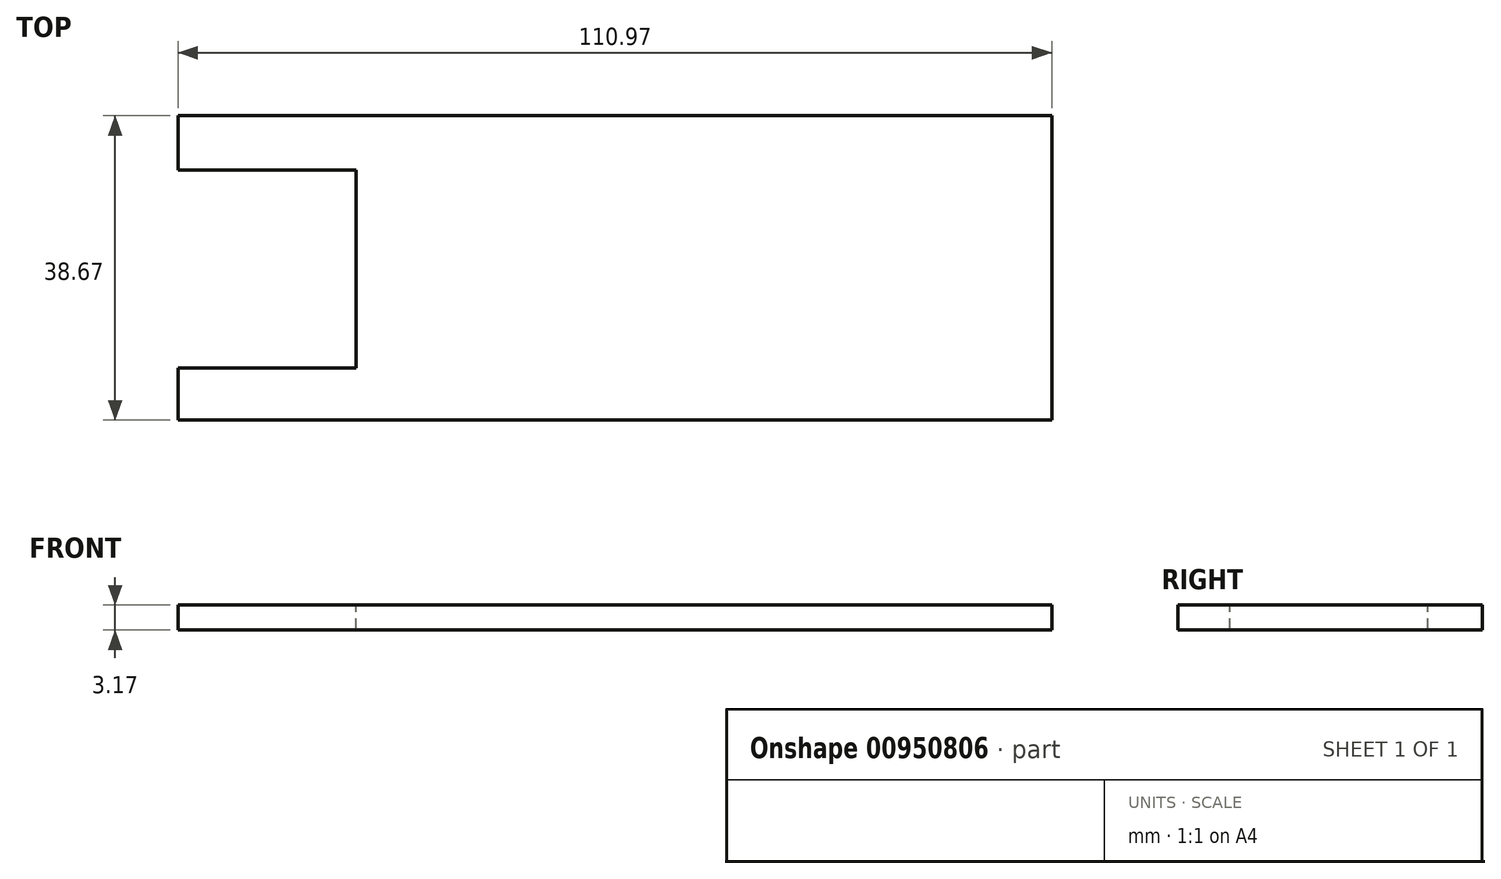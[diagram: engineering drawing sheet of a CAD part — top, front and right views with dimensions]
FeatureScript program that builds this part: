
annotation { "Feature Type Name" : "Feature", "Feature Type Description" : "" }
export const myFeature = defineFeature(function(context is Context, id is Id, definition is map)
    precondition{}
    {
        {
            var Q0;
            Q0=qCreatedBy(makeId("Top.planeOp"),FACE);
            var sketch = newSketch(context, id + "F0", { "sketchPlane" : qUnion([Q0])});
            skLineSegment(sketch, "E0", {"start": v(-43.23, 21.06) * mm, "end": v(45.11, 21.06) * mm});
            skLineSegment(sketch, "E1", {"start": v(45.11, -17.6) * mm, "end": v(45.11, 21.06) * mm});
            skLineSegment(sketch, "E2", {"start": v(45.11, -17.6) * mm, "end": v(-43.23, -17.6) * mm});
            skLineSegment(sketch, "E3", {"start": v(-43.23, -17.6) * mm, "end": v(-43.23, 21.06) * mm});
            skSolve(sketch);
        }
        {
            var Q0;
            Q0=makeQuery(id+"F0.imprint","IMPRINT",FACE,{"disambiguationData":[TD([[makeQuery(id+"F0.imprint","IMPRINT",EDGE,{"derivedFrom":sQuery(id+"F0.wireOp",EDGE,"E0")}),-1.0]])]});
            extrude(context, id + "F1", {"entities" : qUnion([Q0]), "depth" : 3.17 * mm, "offsetDistance" : 25.4 * mm});
        }
        {
            var Q0;
            Q0=makeQuery(id+"F1.opExtrude","CAP_FACE",FACE,{"disambiguationData":[OSD([sQuery(id+"F0.wireOp",EDGE,"E0"),sQuery(id+"F0.wireOp",EDGE,"E1"),sQuery(id+"F0.wireOp",EDGE,"E2"),sQuery(id+"F0.wireOp",EDGE,"E3")])],"isStart":false});
            var sketch = newSketch(context, id + "F2", { "sketchPlane" : qUnion([Q0])});
            skLineSegment(sketch, "E4", {"start": v(-43.23, 21.06) * mm, "end": v(-65.86, 21.06) * mm});
            skLineSegment(sketch, "E5", {"start": v(-65.86, 21.06) * mm, "end": v(-65.86, 14.15) * mm});
            skLineSegment(sketch, "E6", {"start": v(-65.86, 14.15) * mm, "end": v(-43.23, 14.15) * mm});
            skLineSegment(sketch, "E7", {"start": v(-43.23, 14.15) * mm, "end": v(-43.23, 21.06) * mm});
            skSolve(sketch);
        }
        {
            var Q0;
            Q0=makeQuery(id+"F2.imprint","IMPRINT",FACE,{"disambiguationData":[TD([[makeQuery(id+"F2.imprint","IMPRINT",EDGE,{"derivedFrom":sQuery(id+"F2.wireOp",EDGE,"E4")}),1.0]])]});
            extrude(context, id + "F3", {"entities" : qUnion([Q0]), "operationType" : NewBodyOperationType.ADD, "oppositeDirection" : true, "depth" : 3.17 * mm, "offsetDistance" : 25.4 * mm});
        }
        {
            var Q0;
            Q0=makeQuery(id+"F3.boolean.opBoolean","MERGE",FACE,{"derivedFrom":[makeQuery(id+"F1.opExtrude","CAP_FACE",FACE,{"disambiguationData":[OSD([sQuery(id+"F0.wireOp",EDGE,"E0"),sQuery(id+"F0.wireOp",EDGE,"E1"),sQuery(id+"F0.wireOp",EDGE,"E2"),sQuery(id+"F0.wireOp",EDGE,"E3")])],"isStart":false}),makeQuery(id+"F3.opExtrude","CAP_FACE",FACE,{"disambiguationData":[OSD([sQuery(id+"F2.wireOp",EDGE,"E4"),sQuery(id+"F2.wireOp",EDGE,"E5"),sQuery(id+"F2.wireOp",EDGE,"E6"),sQuery(id+"F2.wireOp",EDGE,"E7")])],"isStart":true})]});
            var sketch = newSketch(context, id + "F4", { "sketchPlane" : qUnion([Q0])});
            skLineSegment(sketch, "E8", {"start": v(-43.23, -17.6) * mm, "end": v(-65.86, -17.6) * mm});
            skLineSegment(sketch, "E9", {"start": v(-65.86, -17.6) * mm, "end": v(-65.86, -11) * mm});
            skLineSegment(sketch, "E10", {"start": v(-65.86, -11) * mm, "end": v(-43.23, -11) * mm});
            skSolve(sketch);
        }
        {
            var Q0;
            {var subQ0=sQuery(id+"F4.wireOp",EDGE,"E8");Q0=makeQuery(id+"F4.imprint","IMPRINT",FACE,{"disambiguationData":[TD([[makeQuery(id+"F4.imprint","IMPRINT",EDGE,{"derivedFrom":subQ0}),-1.0]])]});}
            extrude(context, id + "F5", {"entities" : qUnion([Q0]), "operationType" : NewBodyOperationType.ADD, "oppositeDirection" : true, "depth" : 3.17 * mm, "offsetDistance" : 25.4 * mm});
        }
    });
